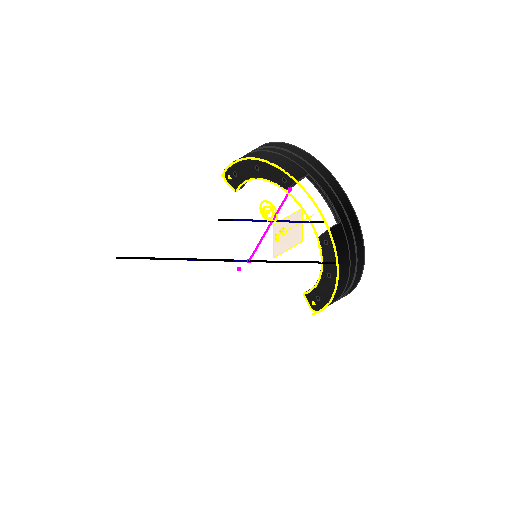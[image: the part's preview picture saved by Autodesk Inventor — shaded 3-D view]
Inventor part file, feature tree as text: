
AUTODESK INVENTOR PART (.ipt)
format: ipt  version: 2022 (Build 260153000, 153)  size: 309,760 bytes
history: native  units: in
note: dims shown in document units (in); Inventor stores cm internally (conversion verified against a paired STEP export)
features: other x10, reference x9, sketch x5, plane x3, extrude x2, projected_geometry x2, revolve x1, fillet x1, hole x1, pattern_circular x1
ambient origin geometry x8: Origin, YZ Plane, XZ Plane, XY Plane, X Axis, Y Axis, Z Axis, Center Point
bodies: Body1 (feature_tree)
feature tree (35):
  other  "Arbeitsachse1"
  plane  "Arbeitsebene4"
  revolve  "Umdrehung1"
  extrude  "Extrusion9"  Depth=0.1969in
  fillet  "Rundung2"  [1 undecoded]
  sketch  "Skizze13"  dims[d41=0.2362in]
  plane  "Arbeitsebene6"
  hole  "Bohrung1"  [1 undecoded]
  pattern_circular  "Runde Anordnung1"  Angle=360.0deg  [1 undecoded]
  sketch  "Skizze17"  dims[d43=0.0236in d44=360.0deg d46=0.3937in d47=0.0in d55=0.1969in d56=0.0118in d68=105.0deg d69=105.0deg d70=0.1102in d71=0.1102in d72=0.2362in d73=0.1969in d74=0.3937in d75=90.0deg d76=0.315in d77=0.8108in d78=4.7244in d79=360.0deg d81=0.1181in d82=0.3543in d83=0.0in]
  other  "Arbeitspunkt2"
  extrude  "Extrusion14"  Depth=0.1181in TaperAngle=0.0deg
  plane  "Arbeitsebene3"
  other  "Arbeitspunkt1"
  sketch  "Skizze10"  dims[d36=0.1575in d37=0.1969in d38=135.0deg]
  reference  "Referenz27"
  reference  "Referenz28"
  sketch  "Skizze11"  dims[d39=0.0118in d40=0.0984in]
  reference  "Referenz29"
  reference  "Referenz30"
  reference  "Referenz31"
  projected_geometry  "Projizierte Kontur8"
  projected_geometry  "Projizierte Kontur9"
  reference  "Referenz37"
  reference  "Referenz38"
  reference  "Referenz39"
  sketch  "Skizze16"  dims[d42=0.4724in]
  reference  "Referenz40"
  other  "Anglerfish_bonne_mamman_m12large_flipped_v0.iam"
  other  "00_Lid_Bonne_Mamman:1"
  other  "00_Coverglass:1"
  other  "Anglerfish_Lightplate_Tosslink:1"
  other  "Matchboxscope_M12_Lensadapter_v0:1"
  other  "00_toslink_launcher_v3:2"
  other  "00_toslink_launcher_v3:1"
note: 3 required parameter values undecoded (feature->parameter linkage not recoverable at this tier; creation-order binding heuristic only, values carry confidence <= 0.55)
